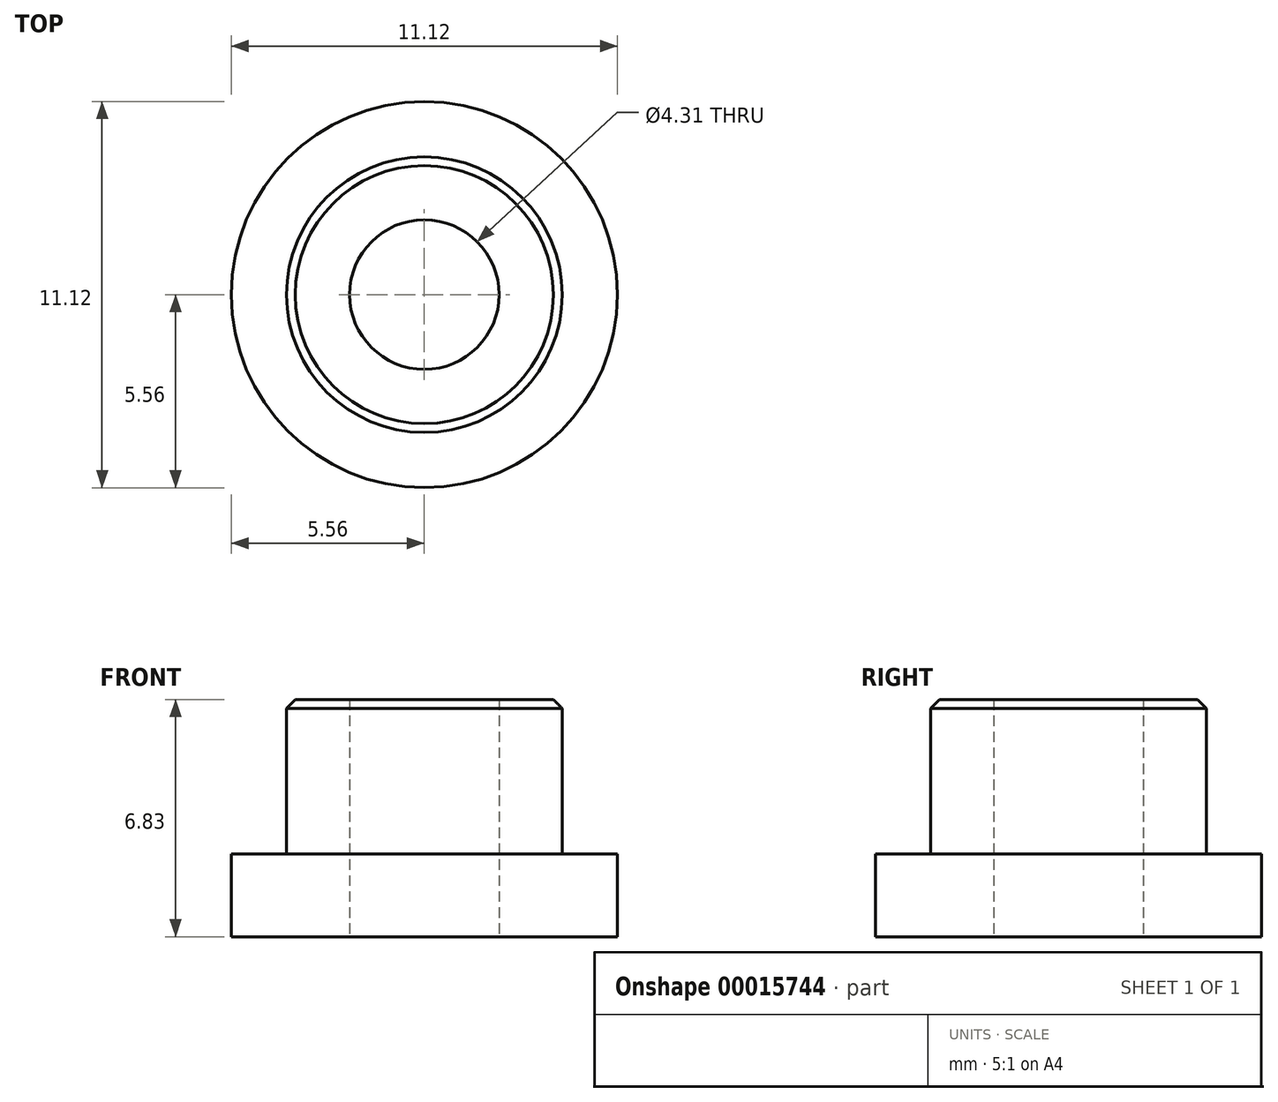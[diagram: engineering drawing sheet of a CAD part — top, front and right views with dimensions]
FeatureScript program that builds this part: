
annotation { "Feature Type Name" : "Feature", "Feature Type Description" : "" }
export const myFeature = defineFeature(function(context is Context, id is Id, definition is map)
    precondition{}
    {
        {
            var Q0;
            Q0=qCreatedBy(makeId("Top.planeOp"),FACE);
            var sketch = newSketch(context, id + "F0", { "sketchPlane" : qUnion([Q0])});
            skCircle(sketch, "E0", {"center": v(0, 0) * mm, "radius": 5.56 * mm});
            skCircle(sketch, "E1", {"center": v(0, 0) * mm, "radius": 2.15 * mm});
            skSolve(sketch);
        }
        {
            var Q0;
            Q0 = qSketchRegion(id + "F0", true);
            extrude(context, id + "F1", {"entities" : qUnion([Q0]), "depth" : 2.38 * mm});
        }
        {
            var Q0;
            Q0=makeQuery(id+"F1.opExtrude","CAP_FACE",FACE,{"disambiguationData":[OSD([sQuery(id+"F0.wireOp",EDGE,"E0"),sQuery(id+"F0.wireOp",EDGE,"E1")])],"isStart":false});
            var sketch = newSketch(context, id + "F2", { "sketchPlane" : qUnion([Q0])});
            skCircle(sketch, "E2", {"center": v(0, 0) * mm, "radius": 2.15 * mm});
            skCircle(sketch, "E3", {"center": v(0, 0) * mm, "radius": 3.97 * mm});
            skSolve(sketch);
        }
        {
            var Q0;
            Q0 = qSketchRegion(id + "F2", true);
            extrude(context, id + "F3", {"entities" : qUnion([Q0]), "operationType" : NewBodyOperationType.ADD, "depth" : 4.44 * mm});
        }
        {
            var Q0;
            Q0=makeQuery(id+"F3.opExtrude","CAP_EDGE",EDGE,{"disambiguationData":[OSD([sQuery(id+"F2.wireOp",EDGE,"E3")])],"isStart":false});
            chamfer(context, id + "F4", {"entities" : qUnion([Q0]), "width" : 0.25 * mm, "tangentPropagation" : true});
        }
    });
